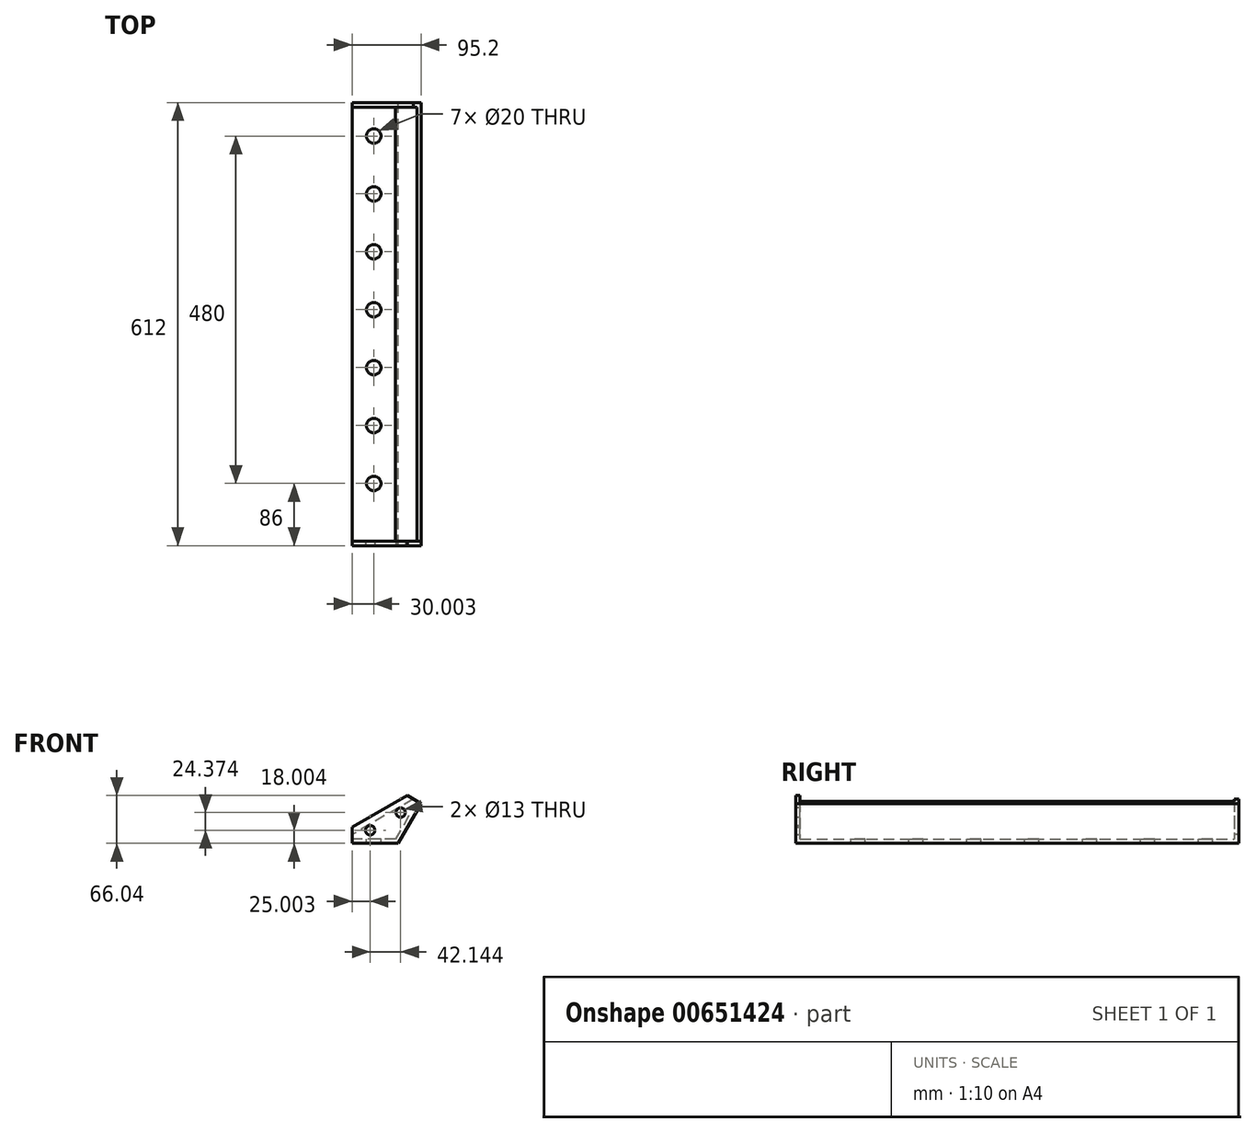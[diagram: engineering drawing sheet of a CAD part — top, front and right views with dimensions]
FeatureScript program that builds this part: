
annotation { "Feature Type Name" : "Feature", "Feature Type Description" : "" }
export const myFeature = defineFeature(function(context is Context, id is Id, definition is map)
    precondition{}
    {
        {
            var Q0;
            Q0=qCreatedBy(makeId("Front.planeOp"),FACE);
            var sketch = newSketch(context, id + "F0", { "sketchPlane" : qUnion([Q0])});
            skLineSegment(sketch, "E0", {"start": v(3.16, -10.39) * mm, "end": v(66.63, -10.39) * mm});
            skLineSegment(sketch, "E1", {"start": v(66.63, -10.39) * mm, "end": v(98.36, 44.58) * mm});
            skLineSegment(sketch, "E2", {"start": v(98.36, 44.58) * mm, "end": v(93.16, 47.58) * mm});
            skLineSegment(sketch, "E3", {"start": v(93.16, 47.58) * mm, "end": v(63.16, -4.39) * mm});
            skLineSegment(sketch, "E4", {"start": v(63.16, -4.39) * mm, "end": v(3.16, -4.39) * mm});
            skLineSegment(sketch, "E5", {"start": v(3.16, -4.39) * mm, "end": v(3.16, -10.39) * mm});
            skSolve(sketch);
        }
        {
            var Q0;
            Q0=qSketchRegion(id+"F0",true);
            extrude(context, id + "F1", {"entities" : qUnion([Q0]), "depth" : 600 * mm, "offsetDistance" : 25 * mm});
        }
        {
            var Q0;
            Q0=makeQuery(id+"F1.opExtrude","CAP_FACE",FACE,{"disambiguationData":[OSD([sQuery(id+"F0.wireOp",EDGE,"E0"),sQuery(id+"F0.wireOp",EDGE,"E1"),sQuery(id+"F0.wireOp",EDGE,"E2"),sQuery(id+"F0.wireOp",EDGE,"E3"),sQuery(id+"F0.wireOp",EDGE,"E4"),sQuery(id+"F0.wireOp",EDGE,"E5")])],"isStart":true});
            var sketch = newSketch(context, id + "F2", { "sketchPlane" : qUnion([Q0])});
            skLineSegment(sketch, "E6", {"start": v(-3.16, 1.61) * mm, "end": v(-3.16, -10.39) * mm});
            skLineSegment(sketch, "E7", {"start": v(-98.36, 44.58) * mm, "end": v(-87.97, 50.58) * mm});
            skLineSegment(sketch, "E8", {"start": v(-87.97, 50.58) * mm, "end": v(-3.16, 1.61) * mm});
            skLineSegment(sketch, "E9", {"start": v(-98.36, 44.58) * mm, "end": v(-66.63, -10.39) * mm});
            skLineSegment(sketch, "E10", {"start": v(-66.63, -10.39) * mm, "end": v(-3.16, -10.39) * mm});
            skSolve(sketch);
        }
        {
            var Q0;
            Q0=makeQuery(id+"F1.opExtrude","SWEPT_FACE",FACE,{"disambiguationData":[OSD([sQuery(id+"F0.wireOp",EDGE,"E4")])]});
            var sketch = newSketch(context, id + "F3", { "sketchPlane" : qUnion([Q0])});
            skCircle(sketch, "E11", {"center": v(33.16, -40) * mm, "radius": 10 * mm});
            skCircle(sketch, "E12", {"center": v(33.16, -120) * mm, "radius": 10 * mm});
            skCircle(sketch, "E13", {"center": v(33.16, -200) * mm, "radius": 10 * mm});
            skCircle(sketch, "E14", {"center": v(33.16, -280) * mm, "radius": 10 * mm});
            skCircle(sketch, "E15", {"center": v(33.16, -360) * mm, "radius": 10 * mm});
            skCircle(sketch, "E16", {"center": v(33.16, -440) * mm, "radius": 10 * mm});
            skCircle(sketch, "E17", {"center": v(33.16, -520) * mm, "radius": 10 * mm});
            skSolve(sketch);
        }
        {
            var Q0;
            Q0=qSketchRegion(id+"F2",true);
            extrude(context, id + "F4", {"entities" : qUnion([Q0]), "operationType" : NewBodyOperationType.ADD, "depth" : 6 * mm, "offsetDistance" : 25 * mm});
        }
        {
            var Q0;
            Q0=makeQuery(id+"F1.opExtrude","CAP_FACE",FACE,{"disambiguationData":[OSD([sQuery(id+"F0.wireOp",EDGE,"E0"),sQuery(id+"F0.wireOp",EDGE,"E1"),sQuery(id+"F0.wireOp",EDGE,"E2"),sQuery(id+"F0.wireOp",EDGE,"E3"),sQuery(id+"F0.wireOp",EDGE,"E4"),sQuery(id+"F0.wireOp",EDGE,"E5")])],"isStart":false});
            var sketch = newSketch(context, id + "F5", { "sketchPlane" : qUnion([Q0])});
            skLineSegment(sketch, "E18", {"start": v(3.16, -10.39) * mm, "end": v(3.16, 11.61) * mm});
            skLineSegment(sketch, "E19", {"start": v(3.16, 11.61) * mm, "end": v(79.35, 55.65) * mm});
            skLineSegment(sketch, "E20", {"start": v(79.35, 55.65) * mm, "end": v(98.36, 44.58) * mm});
            skLineSegment(sketch, "E21", {"start": v(98.36, 44.58) * mm, "end": v(66.63, -10.39) * mm});
            skLineSegment(sketch, "E22", {"start": v(66.63, -10.39) * mm, "end": v(3.16, -10.39) * mm});
            skSolve(sketch);
        }
        {
            var Q0;
            Q0=qSketchRegion(id+"F5",true);
            extrude(context, id + "F6", {"entities" : qUnion([Q0]), "operationType" : NewBodyOperationType.ADD, "depth" : 6 * mm, "offsetDistance" : 25 * mm});
        }
        {
            var Q0;
            Q0=makeQuery(id+"F6.opExtrude","CAP_FACE",FACE,{"disambiguationData":[OSD([sQuery(id+"F5.wireOp",EDGE,"E18"),sQuery(id+"F5.wireOp",EDGE,"E19"),sQuery(id+"F5.wireOp",EDGE,"E20"),sQuery(id+"F5.wireOp",EDGE,"E21"),sQuery(id+"F5.wireOp",EDGE,"E22")])],"isStart":false});
            var sketch = newSketch(context, id + "F7", { "sketchPlane" : qUnion([Q0])});
            skCircle(sketch, "E23", {"center": v(70.3, 31.99) * mm, "radius": 6.5 * mm});
            skCircle(sketch, "E24", {"center": v(28.16, 7.61) * mm, "radius": 6.5 * mm});
            skSolve(sketch);
        }
        {
            var Q0;
            Q0=qSketchRegion(id+"F7",true);
            extrude(context, id + "F8", {"entities" : qUnion([Q0]), "operationType" : NewBodyOperationType.REMOVE, "oppositeDirection" : true, "depth" : 25 * mm, "offsetDistance" : 25 * mm});
        }
        {
            var Q0;
            Q0 = qSketchRegion(id + "F3", true);
            extrude(context, id + "F9", {"entities" : qUnion([Q0]), "operationType" : NewBodyOperationType.REMOVE, "oppositeDirection" : true, "depth" : 25 * mm, "offsetDistance" : 25 * mm});
        }
    });
